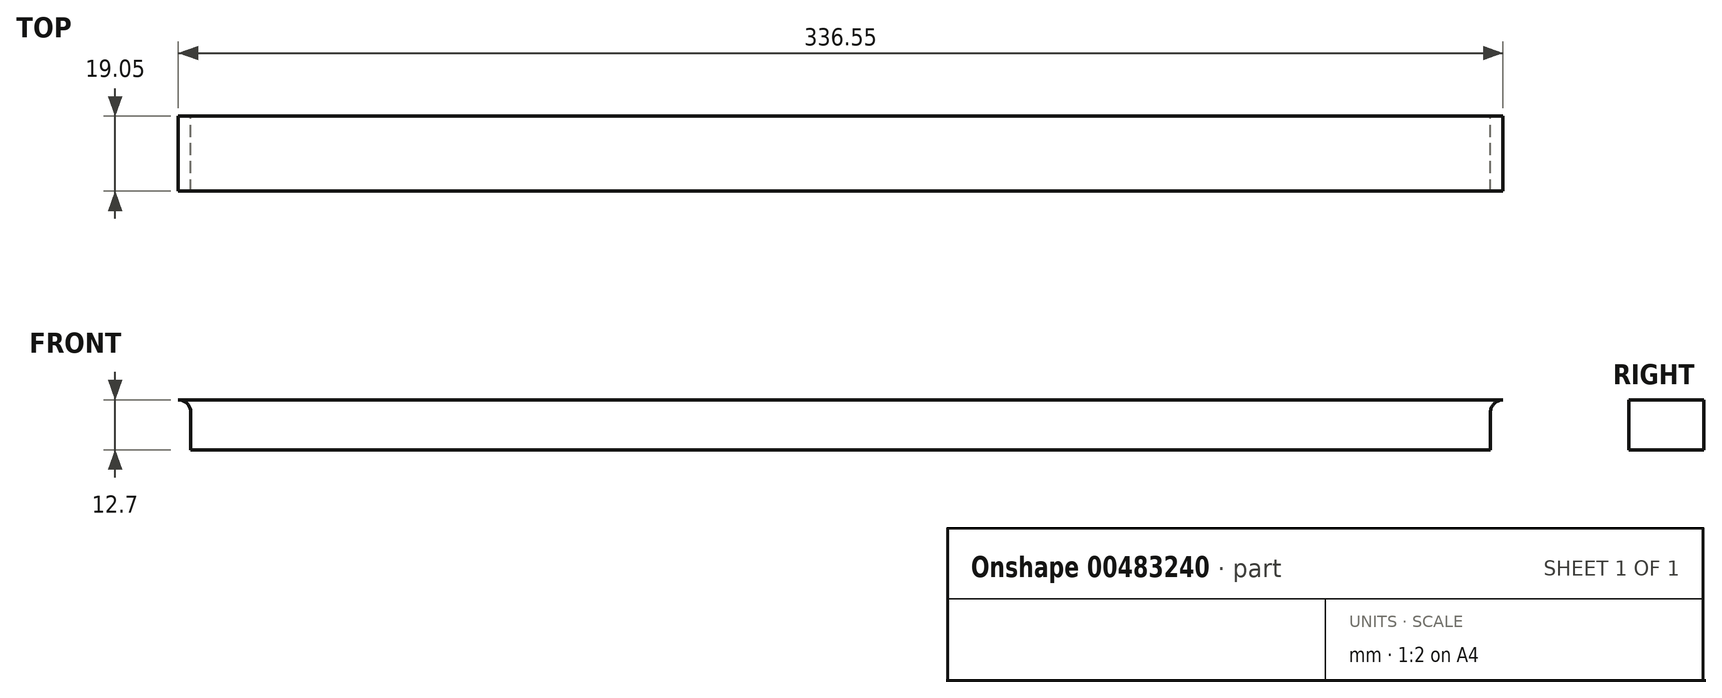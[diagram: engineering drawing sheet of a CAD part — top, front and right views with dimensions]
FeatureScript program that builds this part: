
annotation { "Feature Type Name" : "Feature", "Feature Type Description" : "" }
export const myFeature = defineFeature(function(context is Context, id is Id, definition is map)
    precondition{}
    {
        {
            var Q0;
            Q0=qCreatedBy(makeId("Front.planeOp"),FACE);
            var sketch = newSketch(context, id + "F0", { "sketchPlane" : qUnion([Q0])});
            skLineSegment(sketch, "E0.bottom", {"start": v(67.76, 6.35) * mm, "end": v(-268.79, 6.35) * mm});
            skLineSegment(sketch, "E0.top", {"start": v(64.59, -6.35) * mm, "end": v(-265.61, -6.35) * mm});
            skPoint(sketch, "E0.middle", {"position": v(0, 0) * mm});
            skLineSegment(sketch, "E1", {"start": v(-265.61, 3.17) * mm, "end": v(-265.61, -6.35) * mm});
            skLineSegment(sketch, "E2", {"start": v(64.59, 3.17) * mm, "end": v(64.59, -6.35) * mm});
            skArc(sketch, "E3", {"start": v(67.76, 6.35) * mm, "mid": v(65.52, 5.42) * mm, "end": v(64.59, 3.17) * mm});
            skPoint(sketch, "E4.orphan", {"position": v(268.79, -6.35) * mm});
            skArc(sketch, "E5", {"start": v(-265.61, 3.17) * mm, "mid": v(-266.54, 5.42) * mm, "end": v(-268.79, 6.35) * mm});
            skPoint(sketch, "E6.orphan", {"position": v(-67.76, -6.35) * mm});
            skSolve(sketch);
        }
        {
            var Q0;
            Q0=qSketchRegion(id+"F0",true);
            extrude(context, id + "F1", {"entities" : qUnion([Q0]), "depth" : 19.05 * mm});
        }
    });
